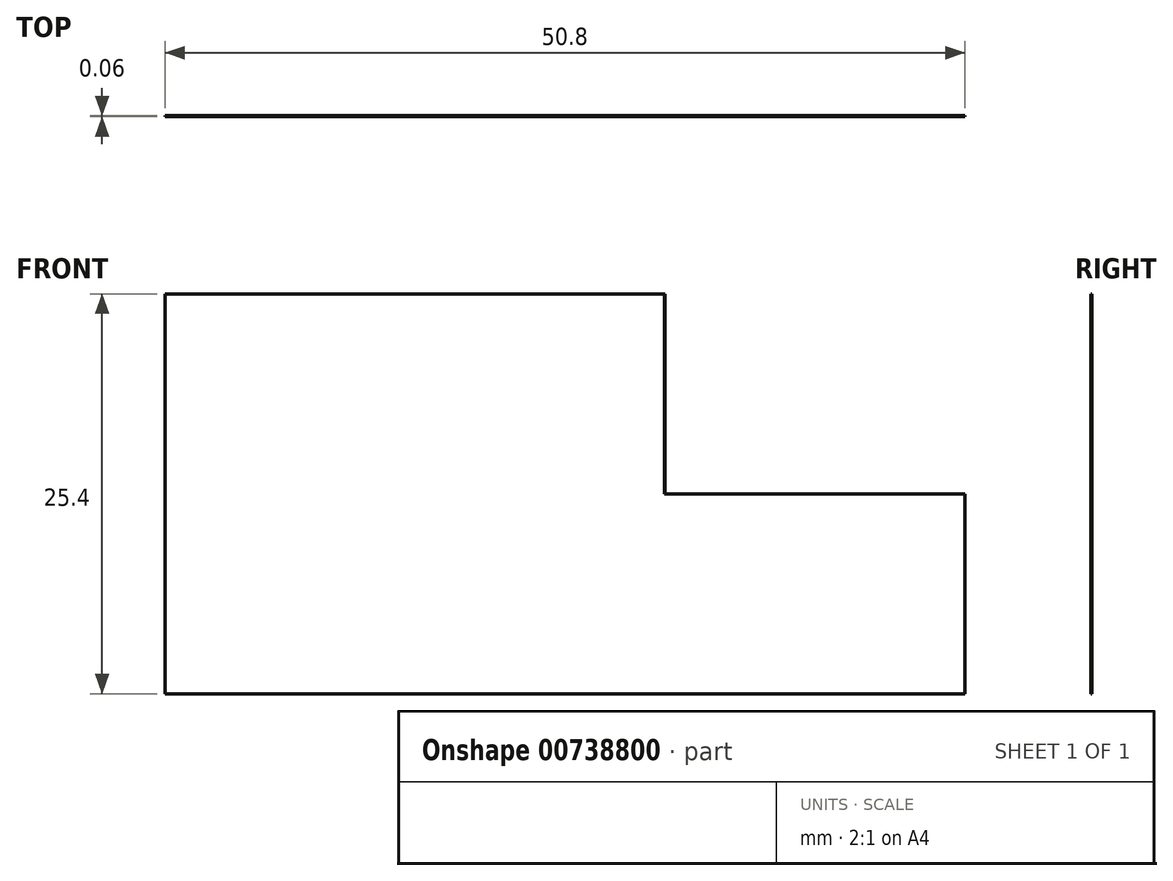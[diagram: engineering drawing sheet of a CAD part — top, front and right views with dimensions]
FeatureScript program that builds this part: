
annotation { "Feature Type Name" : "Feature", "Feature Type Description" : "" }
export const myFeature = defineFeature(function(context is Context, id is Id, definition is map)
    precondition{}
    {
        {
            var Q0;
            Q0=qCreatedBy(makeId("Front.planeOp"),FACE);
            var sketch = newSketch(context, id + "F0", { "sketchPlane" : qUnion([Q0])});
            skLineSegment(sketch, "E0.bottom", {"start": v(-21.06, 7.03) * mm, "end": v(29.74, 7.03) * mm});
            skLineSegment(sketch, "E0.top", {"start": v(-21.06, -18.37) * mm, "end": v(29.74, -18.37) * mm});
            skLineSegment(sketch, "E0.left", {"start": v(-21.06, 7.03) * mm, "end": v(-21.06, -18.37) * mm});
            skLineSegment(sketch, "E0.right", {"start": v(29.74, 7.03) * mm, "end": v(29.74, -18.37) * mm});
            skSolve(sketch);
        }
        {
            var Q0;
            Q0 = qSketchRegion(id + "F0", true);
            extrude(context, id + "F1", {"entities" : qUnion([Q0]), "depth" : 6 / 101.6 * mm, "offsetDistance" : 25.4 * mm});
        }
        {
            var Q0;
            Q0=makeQuery(id+"F1.opExtrude","SWEPT_FACE",FACE,{"disambiguationData":[OSD([sQuery(id+"F0.wireOp",EDGE,"E0.bottom")])]});
            var sketch = newSketch(context, id + "F2", { "sketchPlane" : qUnion([Q0])});
            skLineSegment(sketch, "E1", {"start": v(-14.7, -38.1) * mm, "end": v(10.7, 0) * mm});
            skLineSegment(sketch, "E2", {"start": v(17.04, -38.1) * mm, "end": v(29.74, -19.05) * mm});
            skSolve(sketch);
        }
        {
            var Q0;
            Q0 = qSketchRegion(id + "F2", true);
            var Q1;
            {var subQ5=sQuery(id+"F2.wireOp",EDGE,"E1");Q1=makeQuery(id+"F2.imprint","IMPRINT",FACE,{"disambiguationData":[TD([[makeQuery(id+"F2.imprint","IMPRINT",EDGE,{"derivedFrom":subQ5}),-1.0]])]});}
            extrude(context, id + "F3", {"entities" : qUnion([Q0, Q1]), "operationType" : NewBodyOperationType.REMOVE, "oppositeDirection" : true, "depth" : 12.7 * mm, "offsetDistance" : 25.4 * mm});
        }
    });
